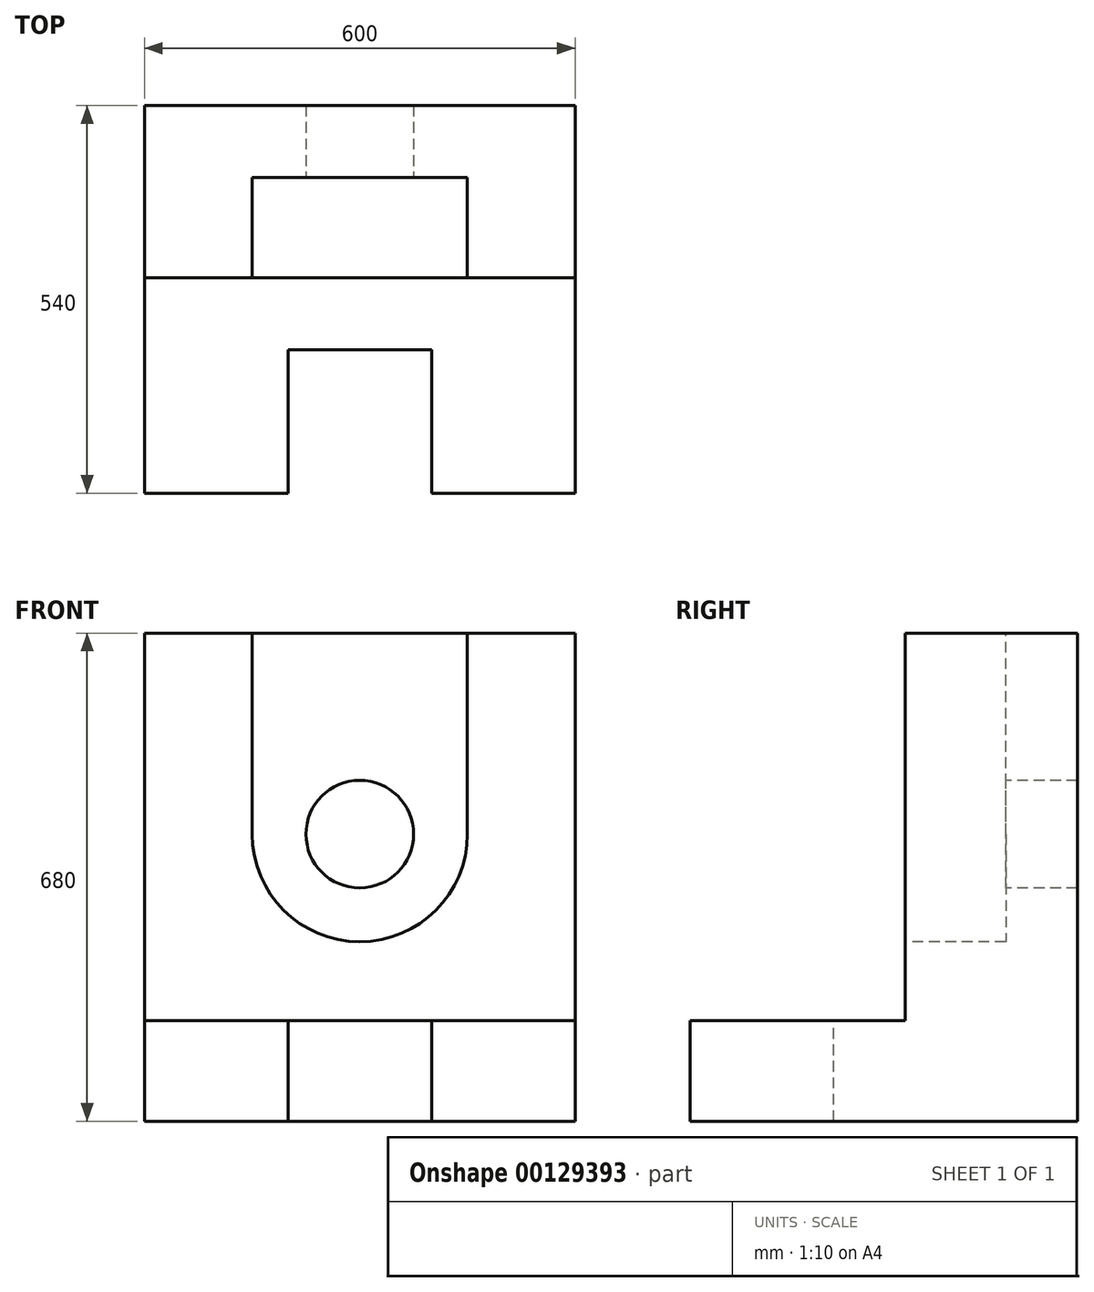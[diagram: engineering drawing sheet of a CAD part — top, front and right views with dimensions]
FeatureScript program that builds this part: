
annotation { "Feature Type Name" : "Feature", "Feature Type Description" : "" }
export const myFeature = defineFeature(function(context is Context, id is Id, definition is map)
    precondition{}
    {
        {
            var Q0;
            Q0=qCreatedBy(makeId("Top.planeOp"),FACE);
            var sketch = newSketch(context, id + "F0", { "sketchPlane" : qUnion([Q0])});
            skLineSegment(sketch, "E0.bottom", {"start": v(-300, -270) * mm, "end": v(300, -270) * mm});
            skLineSegment(sketch, "E0.top", {"start": v(-300, 270) * mm, "end": v(300, 270) * mm});
            skLineSegment(sketch, "E0.left", {"start": v(-300, -270) * mm, "end": v(-300, 270) * mm});
            skLineSegment(sketch, "E0.right", {"start": v(300, -270) * mm, "end": v(300, 270) * mm});
            skPoint(sketch, "E0.middle", {"position": v(0, 0) * mm});
            skSolve(sketch);
        }
        {
            var Q0;
            Q0 = qSketchRegion(id + "F0", true);
            extrude(context, id + "F1", {"entities" : qUnion([Q0]), "depth" : 140 * mm});
        }
        {
            var Q0;
            Q0=makeQuery(id+"F1.opExtrude","CAP_FACE",FACE,{"disambiguationData":[OSD([sQuery(id+"F0.wireOp",EDGE,"E0.bottom"),sQuery(id+"F0.wireOp",EDGE,"E0.top"),sQuery(id+"F0.wireOp",EDGE,"E0.left"),sQuery(id+"F0.wireOp",EDGE,"E0.right")])],"isStart":false});
            var sketch = newSketch(context, id + "F2", { "sketchPlane" : qUnion([Q0])});
            skLineSegment(sketch, "E1.bottom", {"start": v(-100, -70) * mm, "end": v(100, -70) * mm});
            skLineSegment(sketch, "E1.top", {"start": v(-100, -470) * mm, "end": v(100, -470) * mm});
            skLineSegment(sketch, "E1.left", {"start": v(-100, -70) * mm, "end": v(-100, -470) * mm});
            skLineSegment(sketch, "E1.right", {"start": v(100, -70) * mm, "end": v(100, -470) * mm});
            skPoint(sketch, "E1.middle", {"position": v(0, -270) * mm});
            skSolve(sketch);
        }
        {
            var Q0;
            {var subQ0=sQuery(id+"F2.wireOp",EDGE,"E1.bottom");Q0=makeQuery(id+"F2.imprint","IMPRINT",FACE,{"disambiguationData":[TD([[makeQuery(id+"F2.imprint","IMPRINT",EDGE,{"derivedFrom":subQ0}),-1.0]])]});}
            extrude(context, id + "F3", {"entities" : qUnion([Q0]), "operationType" : NewBodyOperationType.REMOVE, "endBound" : BoundingType.THROUGH_ALL, "oppositeDirection" : true, "depth" : 25 * mm});
        }
        {
            var Q0;
            Q0=makeQuery(id+"F1.opExtrude","CAP_FACE",FACE,{"disambiguationData":[OSD([sQuery(id+"F0.wireOp",EDGE,"E0.bottom"),sQuery(id+"F0.wireOp",EDGE,"E0.top"),sQuery(id+"F0.wireOp",EDGE,"E0.left"),sQuery(id+"F0.wireOp",EDGE,"E0.right")])],"isStart":false});
            var sketch = newSketch(context, id + "F4", { "sketchPlane" : qUnion([Q0])});
            skLineSegment(sketch, "E2", {"start": v(-300, 270) * mm, "end": v(300, 270) * mm});
            skLineSegment(sketch, "E3", {"start": v(300, 270) * mm, "end": v(300, 30) * mm});
            skLineSegment(sketch, "E4", {"start": v(300, 30) * mm, "end": v(-300, 30) * mm});
            skPoint(sketch, "E4.endSnap0", {"position": v(-300, 0) * mm});
            skLineSegment(sketch, "E5", {"start": v(-300, 30) * mm, "end": v(-300, 270) * mm});
            skSolve(sketch);
        }
        {
            var Q0;
            Q0=makeQuery(id+"F4.imprint","IMPRINT",FACE,{"disambiguationData":[TD([[makeQuery(id+"F4.imprint","IMPRINT",EDGE,{"derivedFrom":sQuery(id+"F4.wireOp",EDGE,"E2")}),-1.0]])]});
            extrude(context, id + "F5", {"entities" : qUnion([Q0]), "operationType" : NewBodyOperationType.ADD, "depth" : 540 * mm});
        }
        {
            var Q0;
            Q0=makeQuery(id+"F5.opExtrude","SWEPT_FACE",FACE,{"disambiguationData":[OSD([sQuery(id+"F4.wireOp",EDGE,"E4")])]});
            var sketch = newSketch(context, id + "F6", { "sketchPlane" : qUnion([Q0])});
            skLineSegment(sketch, "E6.bottom", {"start": v(-150, 400) * mm, "end": v(150, 400) * mm});
            skLineSegment(sketch, "E6.top", {"start": v(-150, 960) * mm, "end": v(150, 960) * mm});
            skLineSegment(sketch, "E6.left", {"start": v(-150, 400) * mm, "end": v(-150, 960) * mm});
            skLineSegment(sketch, "E6.right", {"start": v(150, 400) * mm, "end": v(150, 960) * mm});
            skPoint(sketch, "E6.middle", {"position": v(0, 680) * mm});
            skSolve(sketch);
        }
        {
            var Q0;
            Q0 = qSketchRegion(id + "F6", true);
            extrude(context, id + "F7", {"entities" : qUnion([Q0]), "operationType" : NewBodyOperationType.REMOVE, "oppositeDirection" : true, "depth" : 140 * mm});
        }
        {
            var Q0;
            Q0=makeQuery(id+"F5.opExtrude","SWEPT_FACE",FACE,{"disambiguationData":[OSD([sQuery(id+"F4.wireOp",EDGE,"E4")])]});
            var sketch = newSketch(context, id + "F8", { "sketchPlane" : qUnion([Q0])});
            skCircle(sketch, "E7", {"center": v(0, 400) * mm, "radius": 150 * mm});
            skSolve(sketch);
        }
        {
            var Q0;
            {var subQ0=sQuery(id+"F6.wireOp",EDGE,"E6.bottom");Q0=makeQuery(id+"FRVbxTngG9eqxgt_1.boolean.opBoolean","MERGE",FACE,{"derivedFrom":[makeQuery(id+"F7.boolean.opBoolean","COPY",FACE,{"derivedFrom":makeQuery(id+"F7.opExtrude","CAP_FACE",FACE,{"disambiguationData":[OSD([subQ0,sQuery(id+"F6.wireOp",EDGE,"E6.top"),sQuery(id+"F6.wireOp",EDGE,"E6.left"),sQuery(id+"F6.wireOp",EDGE,"E6.right")])],"isStart":false})}),makeQuery(id+"FRVbxTngG9eqxgt_1.opExtrude","CAP_FACE",FACE,{"disambiguationData":[OSD([subQ0,sQuery(id+"F8.wireOp",EDGE,"Lp1caX8x-iE2D-JrTE-N9rz-pvWb5QgTeUWj")])],"isStart":false})]});}
            var sketch = newSketch(context, id + "F9", { "sketchPlane" : qUnion([Q0])});
            skCircle(sketch, "E8", {"center": v(0, 400) * mm, "radius": 75 * mm});
            skSolve(sketch);
        }
        {
            var Q0;
            Q0=makeQuery(id+"F9.imprint","IMPRINT",FACE,{"disambiguationData":[TD([[makeQuery(id+"F9.imprint","IMPRINT",EDGE,{"derivedFrom":sQuery(id+"F9.wireOp",EDGE,"E8")}),1.0]])]});
            extrude(context, id + "F10", {"entities" : qUnion([Q0]), "operationType" : NewBodyOperationType.REMOVE, "endBound" : BoundingType.THROUGH_ALL, "oppositeDirection" : true, "depth" : 25 * mm});
        }
        {
            var Q0;
            Q0 = qSketchRegion(id + "F8", true);
            extrude(context, id + "F11", {"entities" : qUnion([Q0]), "operationType" : NewBodyOperationType.REMOVE, "oppositeDirection" : true, "depth" : 140 * mm});
        }
    });
